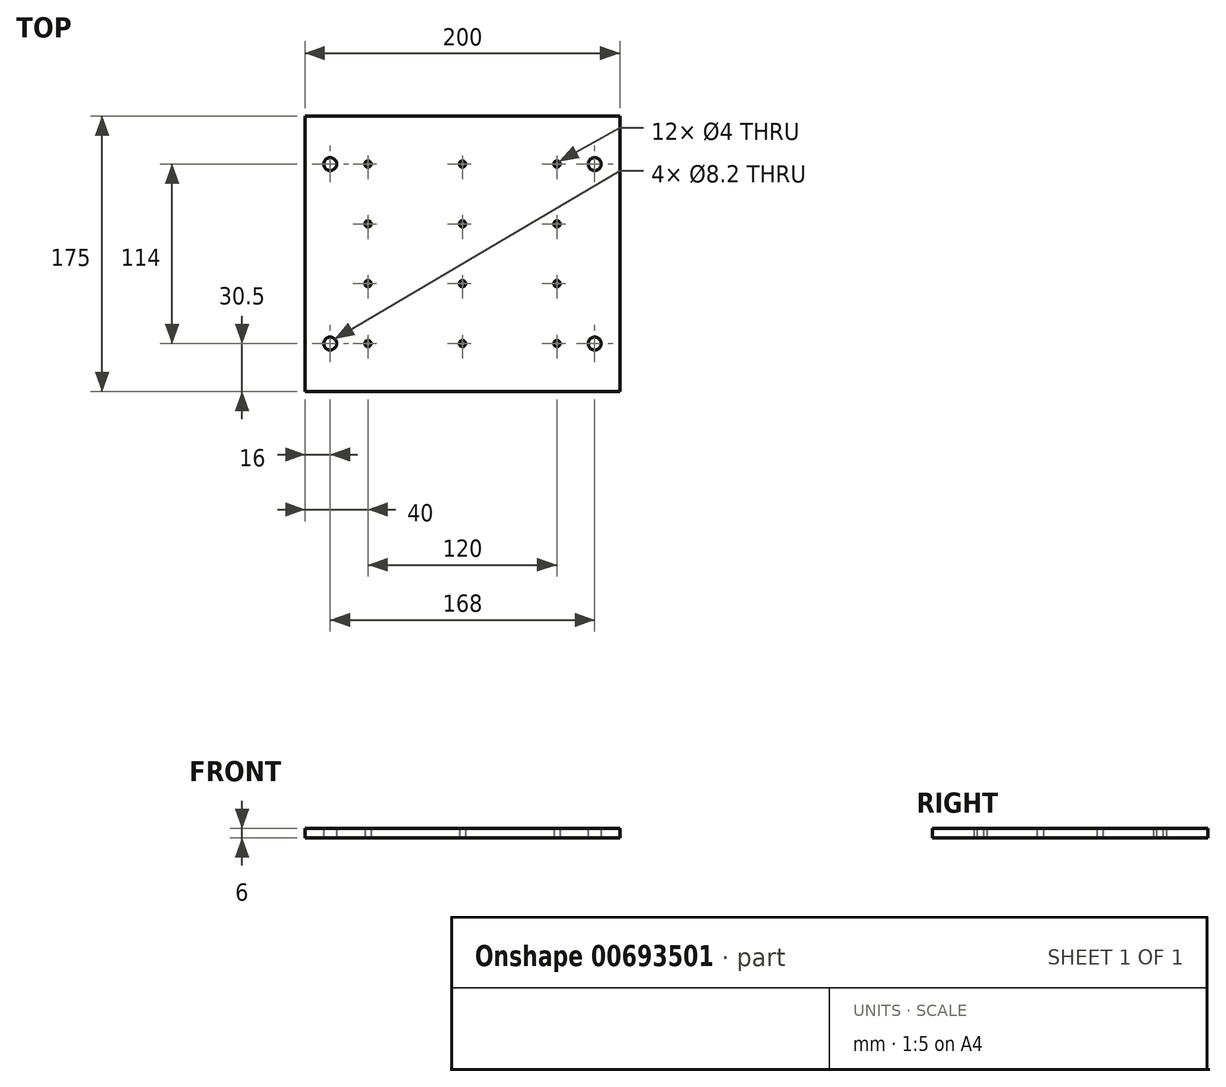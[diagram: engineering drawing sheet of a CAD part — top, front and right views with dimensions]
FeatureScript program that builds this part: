
annotation { "Feature Type Name" : "Feature", "Feature Type Description" : "" }
export const myFeature = defineFeature(function(context is Context, id is Id, definition is map)
    precondition{}
    {
        {
            var Q0;
            Q0=qCreatedBy(makeId("Top.planeOp"),FACE);
            var sketch = newSketch(context, id + "F0", { "sketchPlane" : qUnion([Q0])});
            skLineSegment(sketch, "E0", {"start": v(-79.94, 19) * mm, "end": v(13.07, 19) * mm, "construction": true});
            skLineSegment(sketch, "E1", {"start": v(11.34, 57) * mm, "end": v(-95.78, 57) * mm, "construction": true});
            skLineSegment(sketch, "E2", {"start": v(0, 96.38) * mm, "end": v(0, -5.86) * mm, "construction": true});
            skLineSegment(sketch, "E3", {"start": v(-60, 96.38) * mm, "end": v(-60, -7.01) * mm, "construction": true});
            skLineSegment(sketch, "E4.bottom", {"start": v(100, -87.5) * mm, "end": v(-100, -87.5) * mm});
            skLineSegment(sketch, "E4.top", {"start": v(100, 87.5) * mm, "end": v(-100, 87.5) * mm});
            skLineSegment(sketch, "E4.left", {"start": v(100, -87.5) * mm, "end": v(100, 87.5) * mm});
            skLineSegment(sketch, "E4.right", {"start": v(-100, -87.5) * mm, "end": v(-100, 87.5) * mm});
            skPoint(sketch, "E4.middle", {"position": v(0, 0) * mm});
            skCircle(sketch, "E5", {"center": v(-84, 57) * mm, "radius": 4.1 * mm});
            skCircle(sketch, "E6", {"center": v(0, 57) * mm, "radius": 2 * mm});
            skCircle(sketch, "E7", {"center": v(0, 19) * mm, "radius": 2 * mm});
            skCircle(sketch, "E8", {"center": v(-60, 19) * mm, "radius": 2 * mm});
            skCircle(sketch, "E9", {"center": v(-60, 57) * mm, "radius": 2 * mm});
            skCircle(sketch, "E10.MirrorC", {"center": v(60, 57) * mm, "radius": 2 * mm});
            skCircle(sketch, "E11.MirrorC", {"center": v(60, 19) * mm, "radius": 2 * mm});
            skCircle(sketch, "E12.MirrorC", {"center": v(84, 57) * mm, "radius": 4.1 * mm});
            skCircle(sketch, "E13.MirrorC", {"center": v(-60, -19) * mm, "radius": 2 * mm});
            skCircle(sketch, "E14.MirrorC", {"center": v(-60, -57) * mm, "radius": 2 * mm});
            skCircle(sketch, "E15.MirrorC", {"center": v(-84, -57) * mm, "radius": 4.1 * mm});
            skCircle(sketch, "E16.MirrorC", {"center": v(0, -57) * mm, "radius": 2 * mm});
            skCircle(sketch, "E17.MirrorC", {"center": v(0, -19) * mm, "radius": 2 * mm});
            skCircle(sketch, "E18.MirrorC", {"center": v(60, -19) * mm, "radius": 2 * mm});
            skCircle(sketch, "E19.MirrorC", {"center": v(60, -57) * mm, "radius": 2 * mm});
            skCircle(sketch, "E20.MirrorC", {"center": v(84, -57) * mm, "radius": 4.1 * mm});
            skSolve(sketch);
        }
        {
            var Q0;
            Q0=makeQuery(id+"F0.imprint","IMPRINT",FACE,{"disambiguationData":[TD([[makeQuery(id+"F0.imprint","IMPRINT",EDGE,{"derivedFrom":sQuery(id+"F0.wireOp",EDGE,"E4.bottom")}),-1.0]])]});
            extrude(context, id + "F1", {"entities" : qUnion([Q0]), "depth" : 6 * mm, "offsetDistance" : 25 * mm});
        }
    });
